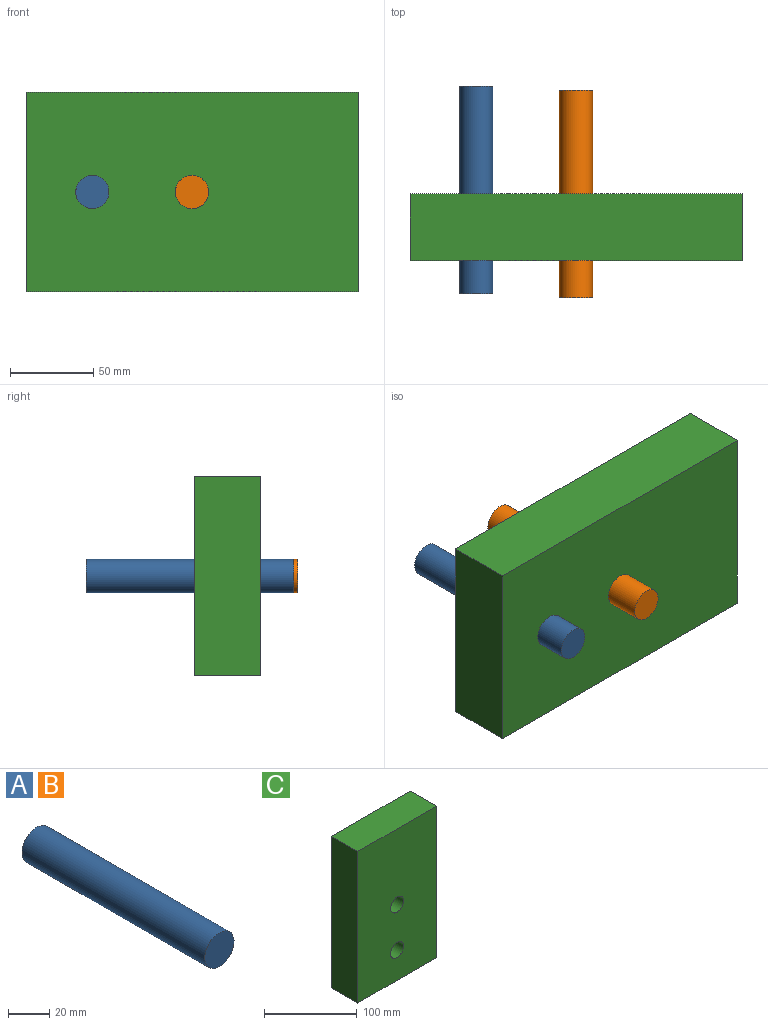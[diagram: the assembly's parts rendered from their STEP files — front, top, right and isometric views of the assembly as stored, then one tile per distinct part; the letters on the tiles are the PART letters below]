
ASSEMBLY  parts=3 mates=2
PART A: 3 faces, bbox 20x125x20 mm
  f0: cylinder r=10mm len=125mm, axis (0,1,0), area 7854mm2, adj f1,f2
  f1: plane 20x20mm, normal (0,-1,0), area 314.2mm2, adj f0
  f2: plane 20x20mm, normal (0,1,0), area 314.2mm2, adj f0
PART B: same geometry as A
PART C: 8 faces, bbox 120x40x200 mm
  f0: plane 200x40mm, normal (1,0,0), area 8000mm2, adj f1,f3,f4,f5
  f1: plane 200x120mm, normal (0,1,0), area 23371.7mm2, adj f0,f2,f4,f5,f6,f7
  f2: plane 200x40mm, normal (-1,0,0), area 8000mm2, adj f1,f3,f4,f5
  f3: plane 200x120mm, normal (0,-1,0), area 23371.7mm2, adj f0,f2,f4,f5,f6,f7
  f4: plane 120x40mm, normal (0,0,1), area 4800mm2, adj f0,f1,f2,f3
  f5: plane 120x40mm, normal (0,0,-1), area 4800mm2, adj f0,f1,f2,f3
  f6: cylinder r=10mm len=40mm, axis (0,-1,0), area 2513.3mm2, adj f1,f3
  f7: cylinder r=10mm len=40mm, axis (0,-1,0), area 2513.3mm2, adj f1,f3
PLACE A rot(axis=(0,1,0),131.9deg) t=(26,-9.53,-19.54)mm
PLACE B t=(86,-11.98,-19.54)mm
PLACE C rot(axis=(0,1,0),90deg) t=(-14,-94.48,-19.54)mm
MATE cylindrical C.f7 <-> A.f0  axis (0,-1,0) through (26,-114.48,-19.54)mm
MATE revolute C.f6 <-> B.f0  axis (0,-1,0) through (86,-74.48,-19.54)mm
